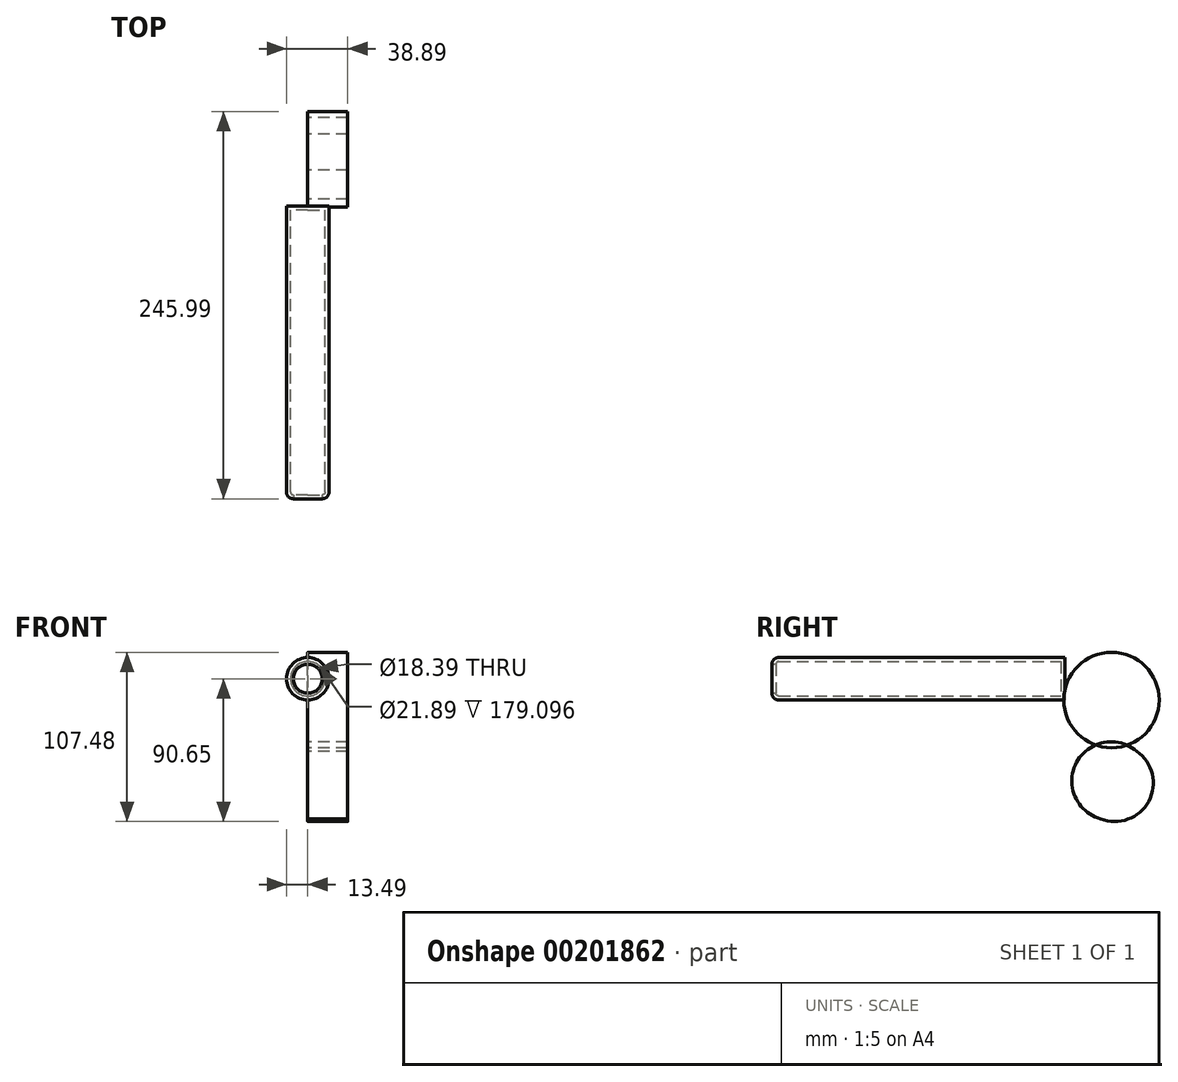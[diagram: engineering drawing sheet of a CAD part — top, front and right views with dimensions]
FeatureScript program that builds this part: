
annotation { "Feature Type Name" : "Feature", "Feature Type Description" : "" }
export const myFeature = defineFeature(function(context is Context, id is Id, definition is map)
    precondition{}
    {
        {
            var Q0;
            Q0=qCreatedBy(makeId("Front.planeOp"),FACE);
            var sketch = newSketch(context, id + "F0", { "sketchPlane" : qUnion([Q0])});
            skCircle(sketch, "E0", {"center": v(0, 0) * mm, "radius": 13.49 * mm});
            skSolve(sketch);
        }
        {
            var Q0;
            Q0 = qSketchRegion(id + "F0", true);
            extrude(context, id + "F1", {"entities" : qUnion([Q0]), "depth" : 185.93 * mm});
        }
        {
            var Q0;
            Q0=makeQuery(id+"F1.opExtrude","CAP_EDGE",EDGE,{"disambiguationData":[OSD([sQuery(id+"F0.wireOp",EDGE,"E0")])],"isStart":false});
            fillet(context, id + "F2", {"entities" : qUnion([Q0]), "radius" : 4.3 * mm, "tangentPropagation" : true, "allowEdgeOverflow" : false});
        }
        {
            var Q0;
            Q0=makeQuery(id+"F1.opExtrude","CAP_FACE",FACE,{"disambiguationData":[OSD([sQuery(id+"F0.wireOp",EDGE,"E0")])],"isStart":false});
            shell(context, id + "F3", {"entities" : qUnion([Q0]), "thickness" : 2.54 * mm});
        }
        {
            var Q0;
            Q0=qCreatedBy(makeId("Right.planeOp"),FACE);
            var sketch = newSketch(context, id + "F4", { "sketchPlane" : qUnion([Q0])});
            skLineSegment(sketch, "E1", {"start": v(0, 11.37) * mm, "end": v(21.4, 11.37) * mm});
            skLineSegment(sketch, "E2", {"start": v(0, -14.06) * mm, "end": v(18.8, -14.06) * mm});
            skLineSegment(sketch, "E3", {"start": v(18.8, -14.06) * mm, "end": v(18.8, -39.49) * mm});
            skLineSegment(sketch, "E4", {"start": v(21.4, 11.37) * mm, "end": v(37.48, 11.37) * mm});
            skLineSegment(sketch, "E5", {"start": v(37.48, 11.37) * mm, "end": v(37.48, -40.53) * mm});
            skCircle(sketch, "E6", {"center": v(29.44, -64.92) * mm, "radius": 24.9 * mm});
            skPoint(sketch, "E6.centerSnap0", {"position": v(29.44, 11.37) * mm});
            skSolve(sketch);
        }
        {
            var Q0;
            Q0 = qSketchRegion(id + "F4", true);
            extrude(context, id + "F5", {"entities" : qUnion([Q0]), "depth" : 25.4 * mm});
        }
        {
            var Q0;
            Q0=qCreatedBy(makeId("Right.planeOp"),FACE);
            var sketch = newSketch(context, id + "F6", { "sketchPlane" : qUnion([Q0])});
            skCircle(sketch, "E7", {"center": v(31.84, -66.2) * mm, "radius": 24.44 * mm});
            skSolve(sketch);
        }
        {
            var Q0;
            Q0=makeQuery(id+"F6.imprint","IMPRINT",FACE,{"disambiguationData":[TD([[makeQuery(id+"F6.imprint","IMPRINT",EDGE,{"derivedFrom":sQuery(id+"F6.wireOp",EDGE,"E7")}),1.0]])]});
            var Q1;
            Q1=makeQuery(id+"F5.opExtrude","CAP_FACE",FACE,{"disambiguationData":[OSD([sQuery(id+"F4.wireOp",EDGE,"E6")])],"isStart":true});
            extrude(context, id + "F7", {"entities" : qUnion([Q0, Q1]), "operationType" : NewBodyOperationType.ADD, "depth" : 25.4 * mm});
        }
        {
            var Q0;
            Q0=qCreatedBy(makeId("Right.planeOp"),FACE);
            var sketch = newSketch(context, id + "F8", { "sketchPlane" : qUnion([Q0])});
            skCircle(sketch, "E8", {"center": v(29.77, -13.47) * mm, "radius": 30.3 * mm});
            skSolve(sketch);
        }
        {
            var Q0;
            Q0 = qSketchRegion(id + "F8", true);
            extrude(context, id + "F9", {"entities" : qUnion([Q0]), "depth" : 25.4 * mm});
        }
    });
